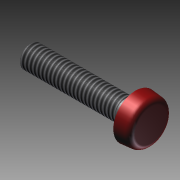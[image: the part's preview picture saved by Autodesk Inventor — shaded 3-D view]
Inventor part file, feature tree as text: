
AUTODESK INVENTOR PART (.ipt)
format: ipt  version: 2011 SP1 (Build 150282100, 282)  size: 105,472 bytes
history: native  units: mm
features: other x7, revolve x1, thread x1, sketch x1
ambient origin geometry x8: Origin, YZ Plane, XZ Plane, XY Plane, X Axis, Y Axis, Z Axis, Center Point
bodies: Solid1 (feature_tree)
feature tree (10):
  revolve  "Revolution1"  [1 undecoded]
  thread  "Thread1"  [1 undecoded]
  other  "AS_XY"
  other  "AS_YZ"
  other  "AS_ZX"
  other  "AS_X"
  other  "AS_Y"
  other  "AS_Z"
  other  "AS_Center"
  sketch  "Skizze_1"  dims[d0=360.0deg d1=17.0705mm d2=0.0mm]
note: 2 required parameter values undecoded (feature->parameter linkage not recoverable at this tier; creation-order binding heuristic only, values carry confidence <= 0.55)